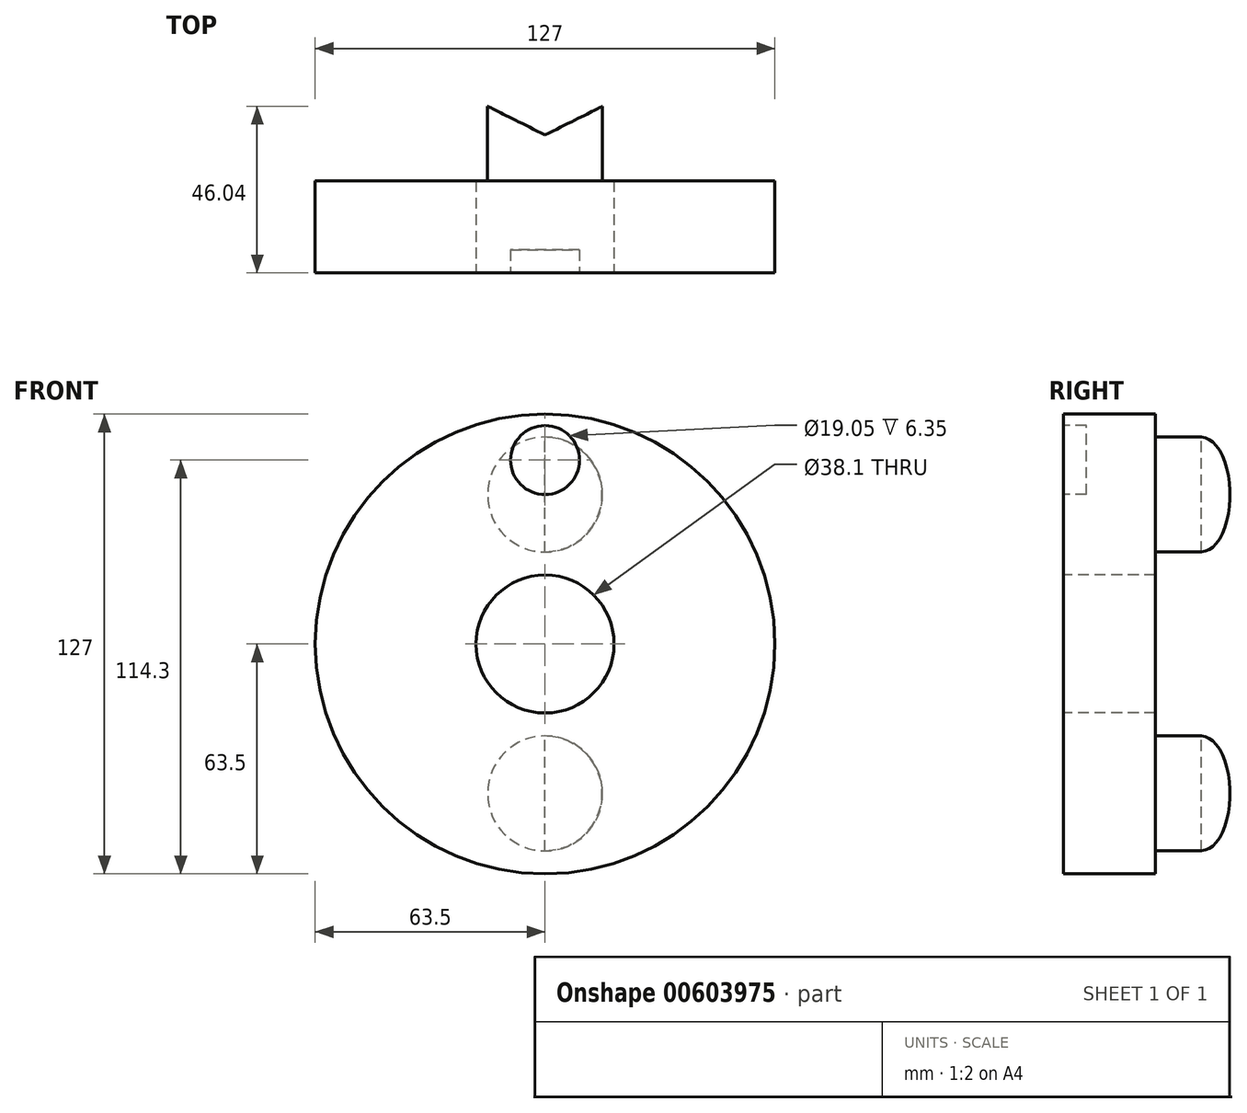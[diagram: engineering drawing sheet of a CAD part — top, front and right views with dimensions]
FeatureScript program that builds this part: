
annotation { "Feature Type Name" : "Feature", "Feature Type Description" : "" }
export const myFeature = defineFeature(function(context is Context, id is Id, definition is map)
    precondition{}
    {
        {
            var Q0;
            Q0=qCreatedBy(makeId("Front.planeOp"),FACE);
            var sketch = newSketch(context, id + "F0", { "sketchPlane" : qUnion([Q0])});
            skCircle(sketch, "E0", {"center": v(0, 0) * mm, "radius": 63.5 * mm});
            skSolve(sketch);
        }
        {
            var Q0;
            Q0 = qSketchRegion(id + "F0", true);
            extrude(context, id + "F1", {"entities" : qUnion([Q0]), "depth" : 25.4 * mm, "offsetDistance" : 25.4 * mm});
        }
        {
            var Q0;
            Q0=makeQuery(id+"F1.opExtrude","CAP_FACE",FACE,{"disambiguationData":[OSD([sQuery(id+"F0.wireOp",EDGE,"E0")])],"isStart":false});
            var sketch = newSketch(context, id + "F2", { "sketchPlane" : qUnion([Q0])});
            skCircle(sketch, "E1", {"center": v(0, 0) * mm, "radius": 50.8 * mm});
            skCircle(sketch, "E2", {"center": v(0, 50.8) * mm, "radius": 9.53 * mm});
            skSolve(sketch);
        }
        {
            var Q0;
            {var subQ0=sQuery(id+"F2.wireOp",EDGE,"E2");var subQ1=sQuery(id+"F2.wireOp",EDGE,"E1");var subQ2=makeQuery(id+"F2.imprint","INTERSECT",VERTEX,{"disambiguationData":[OD(0.0)],"derivedFrom":[subQ1,subQ0]});Q0=makeQuery(id+"F2.imprint","IMPRINT",FACE,{"disambiguationData":[TD([[makeQuery(id+"F2.imprint","IMPRINT",EDGE,{"disambiguationData":[TD([[subQ2,1.0]])],"derivedFrom":subQ1}),1.0]])]});}
            var Q1;
            {var subQ0=sQuery(id+"F2.wireOp",EDGE,"E2");var subQ1=sQuery(id+"F2.wireOp",EDGE,"E1");var subQ2=makeQuery(id+"F2.imprint","INTERSECT",VERTEX,{"disambiguationData":[OD(0.0)],"derivedFrom":[subQ1,subQ0]});Q1=makeQuery(id+"F2.imprint","IMPRINT",FACE,{"disambiguationData":[TD([[makeQuery(id+"F2.imprint","IMPRINT",EDGE,{"disambiguationData":[TD([[subQ2,1.0]])],"derivedFrom":subQ1}),-1.0]])]});}
            extrude(context, id + "F3", {"entities" : qUnion([Q0, Q1]), "operationType" : NewBodyOperationType.REMOVE, "oppositeDirection" : true, "depth" : 6.35 * mm, "offsetDistance" : 25.4 * mm});
        }
        {
            var Q0;
            Q0=makeQuery(id+"F1.opExtrude","CAP_FACE",FACE,{"disambiguationData":[OSD([sQuery(id+"F0.wireOp",EDGE,"E0")])],"isStart":false});
            var sketch = newSketch(context, id + "F4", { "sketchPlane" : qUnion([Q0])});
            skCircle(sketch, "E3", {"center": v(0, 0) * mm, "radius": 19.05 * mm});
            skSolve(sketch);
        }
        {
            var Q0;
            Q0 = qSketchRegion(id + "F4", true);
            extrude(context, id + "F5", {"entities" : qUnion([Q0]), "operationType" : NewBodyOperationType.REMOVE, "oppositeDirection" : true, "depth" : 25.4 * mm, "offsetDistance" : 25.4 * mm});
        }
        {
            var Q0;
            Q0=makeQuery(id+"F1.opExtrude","CAP_FACE",FACE,{"disambiguationData":[OSD([sQuery(id+"F0.wireOp",EDGE,"E0")])],"isStart":true});
            var sketch = newSketch(context, id + "F6", { "sketchPlane" : qUnion([Q0])});
            skCircle(sketch, "E4", {"center": v(0, 41.28) * mm, "radius": 15.88 * mm});
            skCircle(sketch, "E5", {"center": v(0, -41.28) * mm, "radius": 15.88 * mm});
            skSolve(sketch);
        }
        {
            var Q0;
            Q0=makeQuery(id+"F6.imprint","IMPRINT",FACE,{"disambiguationData":[TD([[makeQuery(id+"F6.imprint","IMPRINT",EDGE,{"derivedFrom":sQuery(id+"F6.wireOp",EDGE,"E4")}),1.0]])]});
            var Q1;
            Q1=makeQuery(id+"F6.imprint","IMPRINT",FACE,{"disambiguationData":[TD([[makeQuery(id+"F6.imprint","IMPRINT",EDGE,{"derivedFrom":sQuery(id+"F6.wireOp",EDGE,"E5")}),1.0]])]});
            extrude(context, id + "F7", {"entities" : qUnion([Q0, Q1]), "operationType" : NewBodyOperationType.ADD, "depth" : 25.4 * mm, "offsetDistance" : 25.4 * mm});
        }
        {
            var Q0;
            Q0=makeQuery(id+"F7.opExtrude","CAP_FACE",FACE,{"disambiguationData":[OSD([sQuery(id+"F6.wireOp",EDGE,"E4")])],"isStart":false});
            var sketch = newSketch(context, id + "F8", { "sketchPlane" : qUnion([Q0])});
            skLineSegment(sketch, "E6", {"start": v(0, 57.15) * mm, "end": v(0, 25.4) * mm});
            skSolve(sketch);
        }
        {
            var Q0;
            Q0=qCreatedBy(makeId("Top.planeOp"),FACE);
            var sketch = newSketch(context, id + "F9", { "sketchPlane" : qUnion([Q0])});
            skLineSegment(sketch, "E7", {"start": v(0, 25.4) * mm, "end": v(25.4, 25.4) * mm});
            skLineSegment(sketch, "E8", {"start": v(0, 25.4) * mm, "end": v(-25.4, 25.4) * mm});
            skLineSegment(sketch, "E9", {"start": v(-25.4, 25.4) * mm, "end": v(0, 12.7) * mm});
            skLineSegment(sketch, "E10", {"start": v(0, 12.7) * mm, "end": v(25.4, 25.4) * mm});
            skSolve(sketch);
        }
        {
            var Q0;
            Q0 = qSketchRegion(id + "F9", true);
            extrude(context, id + "F10", {"entities" : qUnion([Q0]), "operationType" : NewBodyOperationType.REMOVE, "endBound" : BoundingType.SYMMETRIC, "oppositeDirection" : true, "depth" : 203.2 * mm, "offsetDistance" : 25.4 * mm});
        }
    });
